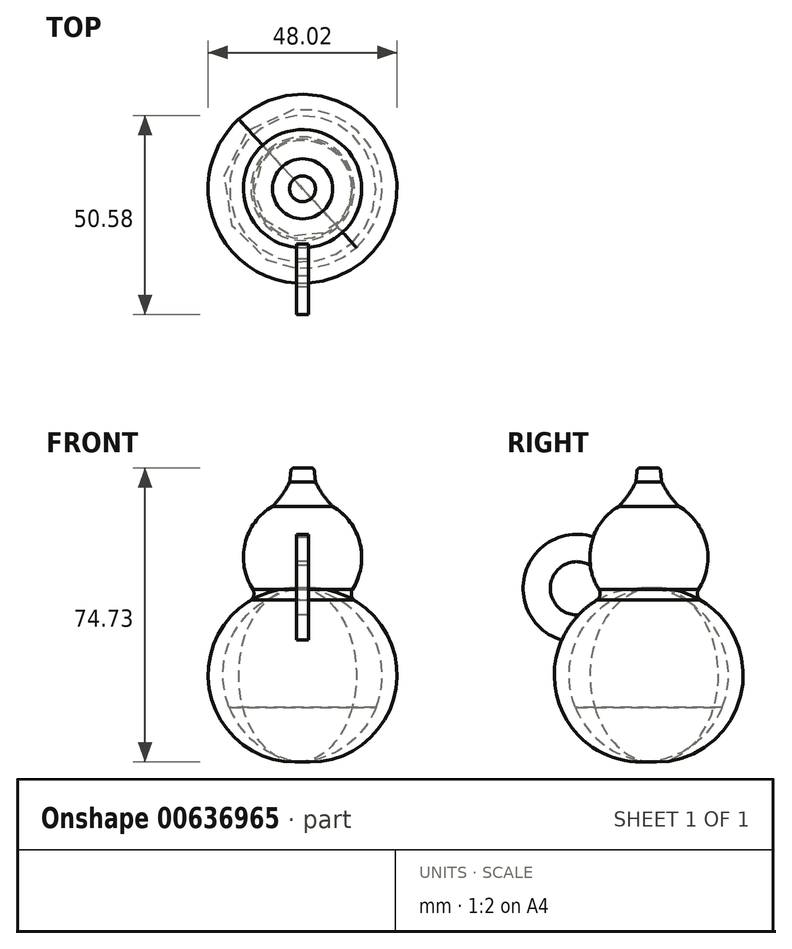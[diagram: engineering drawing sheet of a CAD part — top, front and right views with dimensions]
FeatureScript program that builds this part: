
annotation { "Feature Type Name" : "Feature", "Feature Type Description" : "" }
export const myFeature = defineFeature(function(context is Context, id is Id, definition is map)
    precondition{}
    {
        {
            var Q0;
            Q0=qCreatedBy(makeId("Front.planeOp"),FACE);
            var sketch = newSketch(context, id + "F0", { "sketchPlane" : qUnion([Q0])});
            skLineSegment(sketch, "E0", {"start": v(0, 48.88) * mm, "end": v(0, -48.28) * mm});
            skArc(sketch, "E1", {"start": v(0, 22.9) * mm, "mid": v(-15.03, 7.87) * mm, "end": v(0, -7.16) * mm});
            skArc(sketch, "E2", {"start": v(-3.48, 25.5) * mm, "mid": v(-3.16, 28.03) * mm, "end": v(-2.92, 30.58) * mm});
            skLineSegment(sketch, "E3", {"start": v(-2.92, 30.58) * mm, "end": v(0, 30.58) * mm});
            skArc(sketch, "E4", {"start": v(0, 0) * mm, "mid": v(-24, -22.03) * mm, "end": v(0, -44.07) * mm});
            skArc(sketch, "E5", {"start": v(-13.14, -3) * mm, "mid": v(-12.38, -1.56) * mm, "end": v(-12.8, 0) * mm});
            skArc(sketch, "E6", {"start": v(-7.63, 20.82) * mm, "mid": v(-5.2, 23.74) * mm, "end": v(-3.28, 27) * mm});
            skSolve(sketch);
        }
        {
            var Q0;
            Q0 = qSketchRegion(id + "F0", true);
            var Q1;
            Q1=sQuery(id+"F0.wireOp",EDGE,"E0");
            revolve(context, id + "F1", {"entities" : qUnion([Q0]), "axis" : qUnion([Q1]), "revolveType" : RevolveType.FULL});
        }
        {
            var Q0;
            Q0=makeQuery(id+"F1.opRevolve","SWEPT_EDGE",EDGE,{"disambiguationData":[OSD([sQuery(id+"F0.wireOp",EDGE,"E2"),sQuery(id+"F0.wireOp",EDGE,"E3")])]});
            fillet(context, id + "F2", {"entities" : qUnion([Q0]), "radius" : 0.76 * mm, "tangentPropagation" : true, "allowEdgeOverflow" : false});
        }
        {
            var Q0;
            Q0=qCreatedBy(makeId("Right.planeOp"),FACE);
            var sketch = newSketch(context, id + "F3", { "sketchPlane" : qUnion([Q0])});
            skCircle(sketch, "E7", {"center": v(-18.22, 0) * mm, "radius": 13.72 * mm});
            skCircle(sketch, "E8", {"center": v(-18.22, 0) * mm, "radius": 6.77 * mm});
            skSolve(sketch);
        }
        {
            var Q0;
            Q0 = qSketchRegion(id + "F3", true);
            extrude(context, id + "F4", {"entities" : qUnion([Q0]), "operationType" : NewBodyOperationType.ADD, "depth" : 1.52 * mm, "offsetDistance" : 25.4 * mm, "hasSecondDirection" : true, "secondDirectionOppositeDirection" : true, "secondDirectionDepth" : 1.52 * mm});
        }
    });
